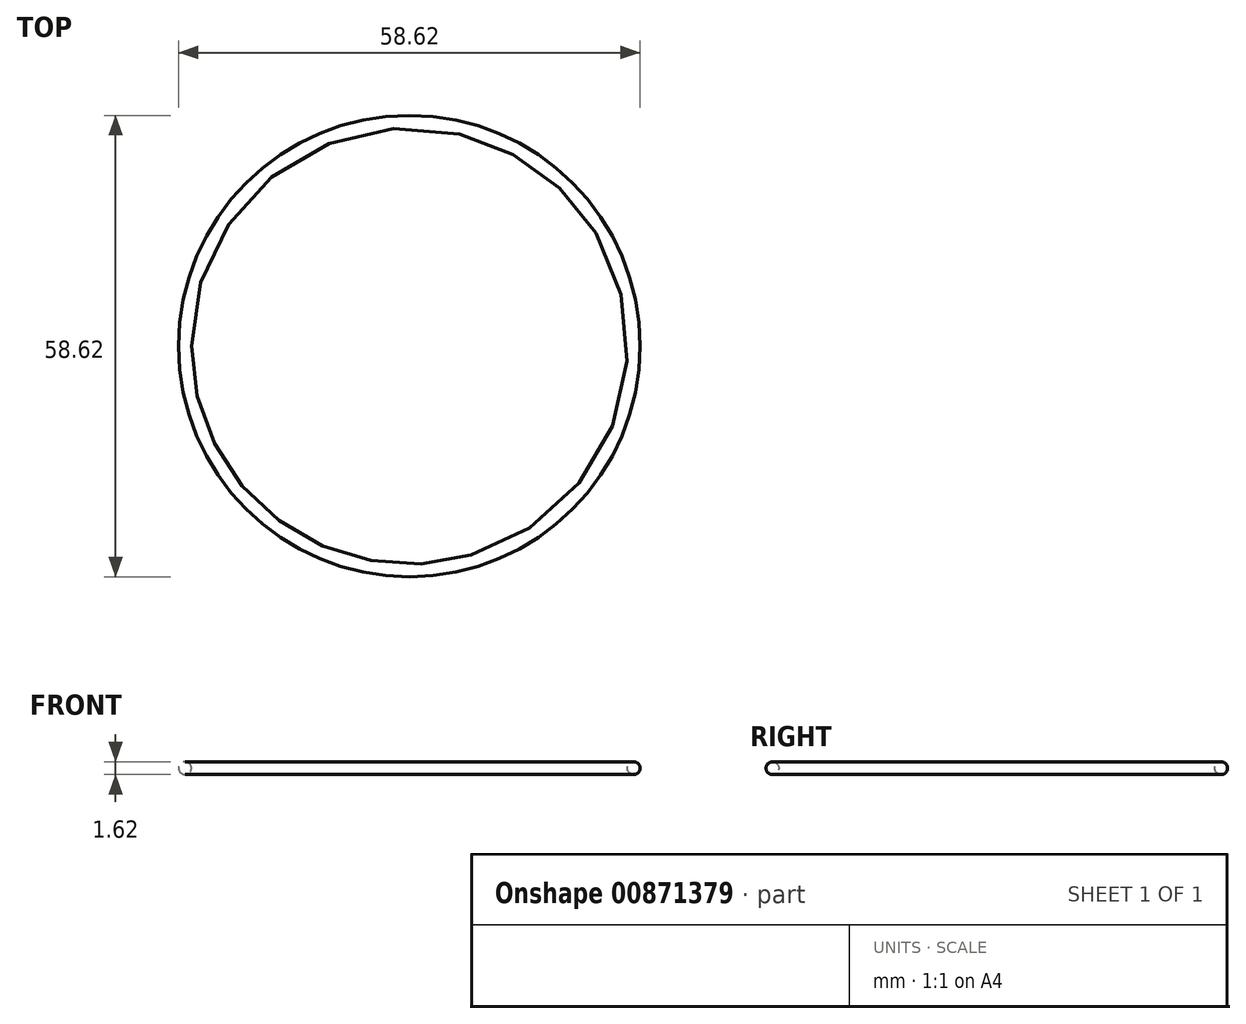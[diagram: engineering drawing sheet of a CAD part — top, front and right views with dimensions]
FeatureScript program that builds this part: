
annotation { "Feature Type Name" : "Feature", "Feature Type Description" : "" }
export const myFeature = defineFeature(function(context is Context, id is Id, definition is map)
    precondition{}
    {
        {
            var Q0;
            Q0=qCreatedBy(makeId("Front.planeOp"),FACE);
            var sketch = newSketch(context, id + "F0", { "sketchPlane" : qUnion([Q0])});
            skCircle(sketch, "E0", {"center": v(28.5, 0) * mm, "radius": 0.81 * mm});
            skLineSegment(sketch, "E1", {"start": v(0, 0) * mm, "end": v(0, 20.74) * mm, "construction": true});
            skSolve(sketch);
        }
        {
            var Q0;
            Q0=makeQuery(id+"F0.imprint","IMPRINT",FACE,{"disambiguationData":[TD([[makeQuery(id+"F0.imprint","IMPRINT",EDGE,{"derivedFrom":sQuery(id+"F0.wireOp",EDGE,"E0")}),1.0]])]});
            var Q1;
            Q1=sQuery(id+"F0.wireOp",EDGE,"E1");
            revolve(context, id + "F1", {"surfaceOperationType" : NewSurfaceOperationType.NEW, "entities" : qUnion([Q0]), "axis" : qUnion([Q1]), "revolveType" : RevolveType.FULL});
        }
    });
